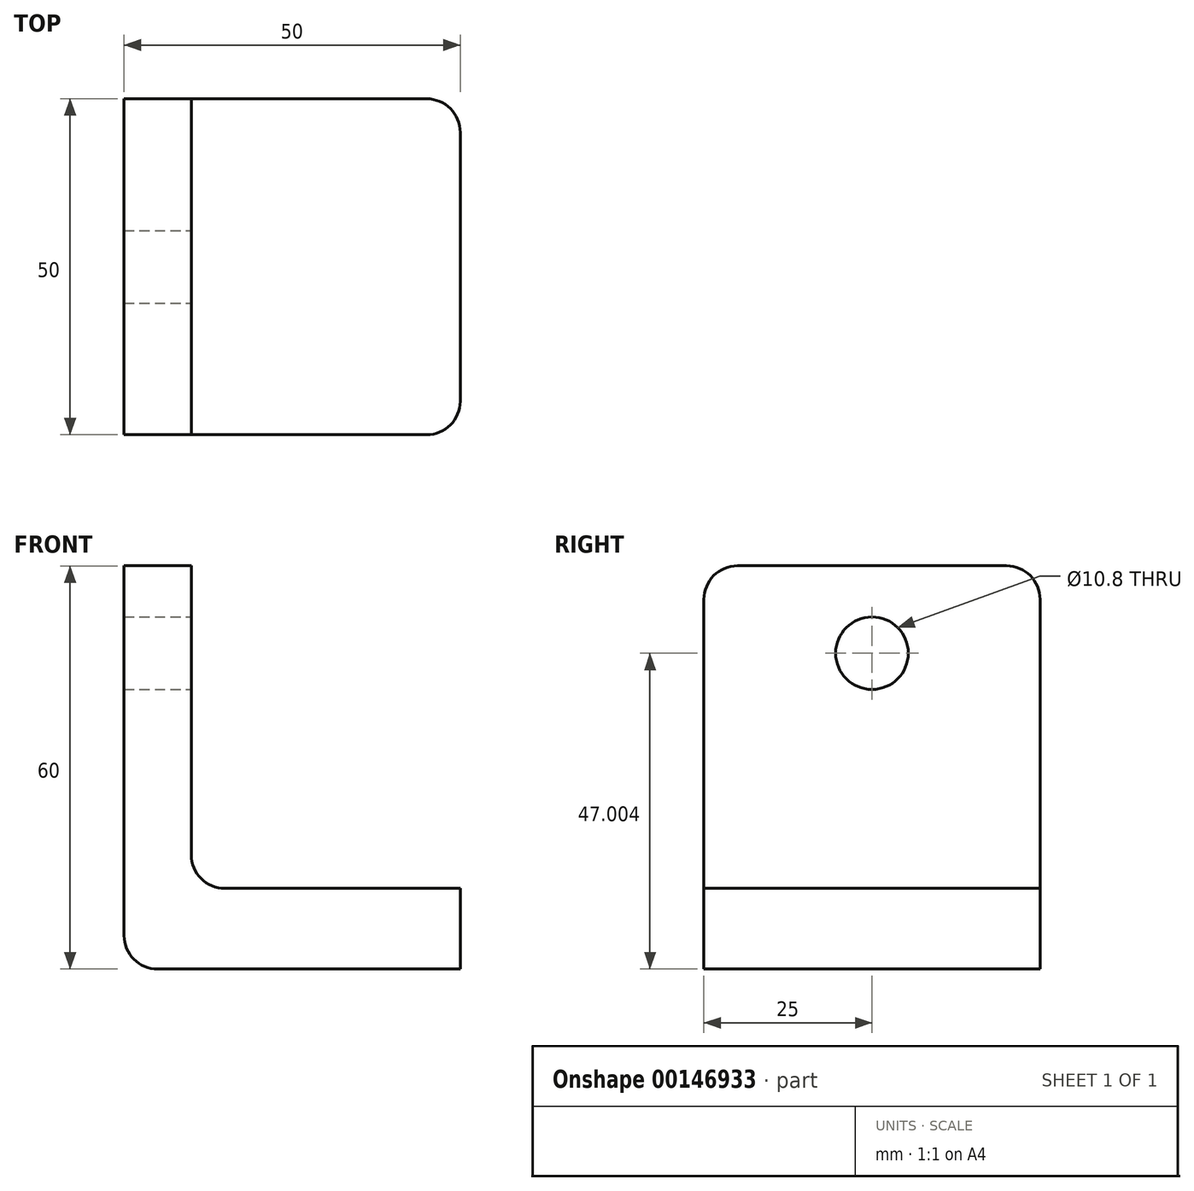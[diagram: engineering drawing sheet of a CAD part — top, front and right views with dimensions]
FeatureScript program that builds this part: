
annotation { "Feature Type Name" : "Feature", "Feature Type Description" : "" }
export const myFeature = defineFeature(function(context is Context, id is Id, definition is map)
    precondition{}
    {
        {
            var Q0;
            Q0=qCreatedBy(makeId("Front.planeOp"),FACE);
            var sketch = newSketch(context, id + "F0", { "sketchPlane" : qUnion([Q0])});
            skLineSegment(sketch, "E0", {"start": v(-35.94, 37.93) * mm, "end": v(-35.94, -22.07) * mm});
            skLineSegment(sketch, "E1", {"start": v(-35.94, -22.07) * mm, "end": v(14.06, -22.07) * mm});
            skLineSegment(sketch, "E2", {"start": v(14.06, -22.07) * mm, "end": v(14.06, -10.07) * mm});
            skLineSegment(sketch, "E3", {"start": v(14.06, -10.07) * mm, "end": v(-25.94, -10.07) * mm});
            skLineSegment(sketch, "E4", {"start": v(-25.94, -10.07) * mm, "end": v(-25.94, 37.93) * mm});
            skLineSegment(sketch, "E5", {"start": v(-25.94, 37.93) * mm, "end": v(-35.94, 37.93) * mm});
            skSolve(sketch);
        }
        {
            var Q0;
            Q0=makeQuery(id+"F0.imprint","IMPRINT",FACE,{"disambiguationData":[TD([[makeQuery(id+"F0.imprint","IMPRINT",EDGE,{"derivedFrom":sQuery(id+"F0.wireOp",EDGE,"E0")}),1.0]])]});
            extrude(context, id + "F1", {"entities" : qUnion([Q0]), "endBound" : BoundingType.SYMMETRIC, "depth" : 50 * mm});
        }
        {
            var Q0;
            Q0=makeQuery(id+"F1.opExtrude","SWEPT_FACE",FACE,{"disambiguationData":[OSD([sQuery(id+"F0.wireOp",EDGE,"E4")])]});
            var sketch = newSketch(context, id + "F2", { "sketchPlane" : qUnion([Q0])});
            skLineSegment(sketch, "E6", {"start": v(0, -36.56) * mm, "end": v(0, 51.63) * mm, "construction": true});
            skLineSegment(sketch, "E7", {"start": v(-57.76, -10.25) * mm, "end": v(61.17, -10.07) * mm, "construction": true});
            skCircle(sketch, "E8", {"center": v(0, 24.93) * mm, "radius": 5.4 * mm});
            skSolve(sketch);
        }
        {
            var Q0;
            Q0=sQuery(id+"F2.wireOp",VERTEX,"E8.center");
            var Q1;
            Q1=makeQuery(id+"F1.opExtrude","SWEPT_BODY",BODY,{"disambiguationData":[OSD([sQuery(id+"F0.wireOp",EDGE,"E0"),sQuery(id+"F0.wireOp",EDGE,"E1"),sQuery(id+"F0.wireOp",EDGE,"E2"),sQuery(id+"F0.wireOp",EDGE,"E3"),sQuery(id+"F0.wireOp",EDGE,"E4"),sQuery(id+"F0.wireOp",EDGE,"E5")])]});
            hole(context, id + "F3", {"style" : HoleStyle.SIMPLE, "endStyle" : HoleEndStyle.THROUGH, "holeDiameter" : 10.8 * mm, "locations" : qUnion([Q0]), "scope" : qUnion([Q1]), "isTappedThrough" : true});
        }
        {
            var Q0;
            Q0=makeQuery(id+"F1.opExtrude","CAP_EDGE",EDGE,{"disambiguationData":[OSD([sQuery(id+"F0.wireOp",EDGE,"E5")])],"isStart":false});
            var Q1;
            Q1=makeQuery(id+"F1.opExtrude","CAP_EDGE",EDGE,{"disambiguationData":[OSD([sQuery(id+"F0.wireOp",EDGE,"E5")])],"isStart":true});
            var Q2;
            Q2=makeQuery(id+"F1.opExtrude","CAP_EDGE",EDGE,{"disambiguationData":[OSD([sQuery(id+"F0.wireOp",EDGE,"E2")])],"isStart":false});
            var Q3;
            Q3=makeQuery(id+"F1.opExtrude","CAP_EDGE",EDGE,{"disambiguationData":[OSD([sQuery(id+"F0.wireOp",EDGE,"E2")])],"isStart":true});
            var Q4;
            Q4=makeQuery(id+"F1.opExtrude","SWEPT_EDGE",EDGE,{"disambiguationData":[OSD([sQuery(id+"F0.wireOp",EDGE,"E0"),sQuery(id+"F0.wireOp",EDGE,"E1")])]});
            var Q5;
            Q5=makeQuery(id+"F1.opExtrude","SWEPT_EDGE",EDGE,{"disambiguationData":[OSD([sQuery(id+"F0.wireOp",EDGE,"E3"),sQuery(id+"F0.wireOp",EDGE,"E4")])]});
            fillet(context, id + "F4", {"entities" : qUnion([Q0, Q1, Q2, Q3, Q4, Q5]), "radius" : 5 * mm, "tangentPropagation" : true, "allowEdgeOverflow" : false});
        }
    });
